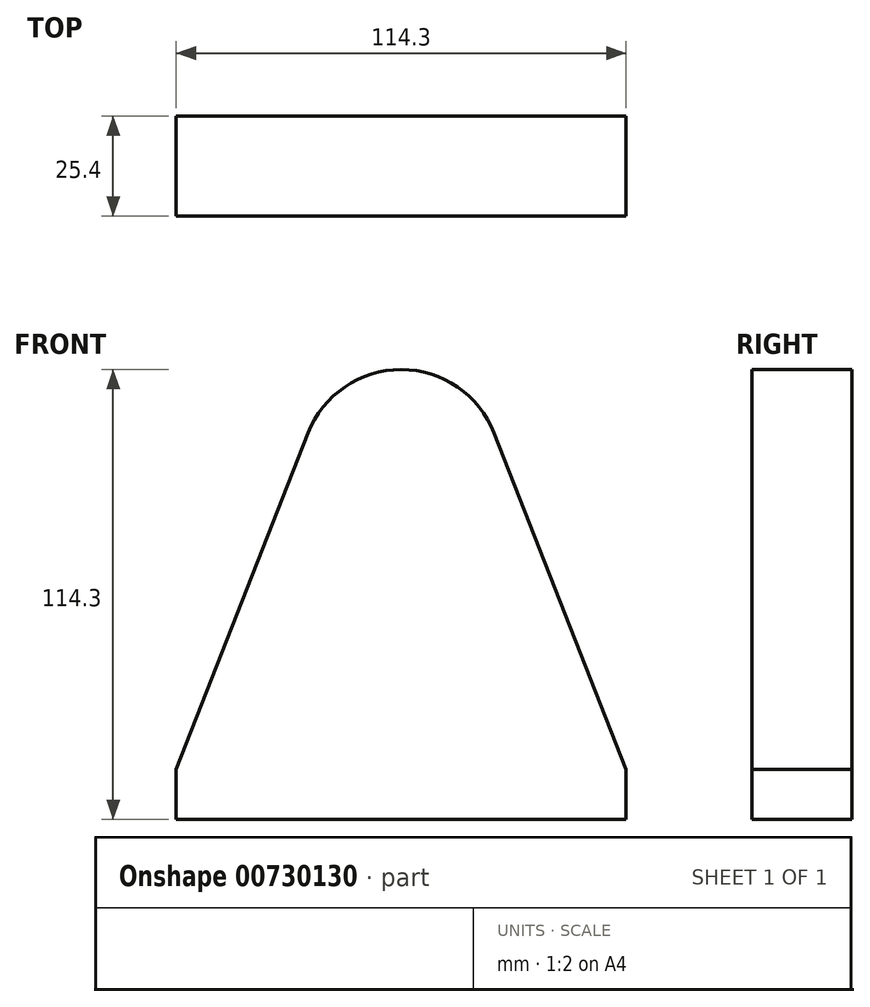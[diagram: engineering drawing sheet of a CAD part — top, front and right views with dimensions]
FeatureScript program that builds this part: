
annotation { "Feature Type Name" : "Feature", "Feature Type Description" : "" }
export const myFeature = defineFeature(function(context is Context, id is Id, definition is map)
    precondition{}
    {
        {
            var Q0;
            Q0=qCreatedBy(makeId("Front.planeOp"),FACE);
            var sketch = newSketch(context, id + "F0", { "sketchPlane" : qUnion([Q0])});
            skArc(sketch, "E0", {"start": v(23.65, 9.27) * mm, "mid": v(0, 25.4) * mm, "end": v(-23.65, 9.27) * mm});
            skLineSegment(sketch, "E1", {"start": v(-57.15, -88.9) * mm, "end": v(57.15, -88.9) * mm});
            skLineSegment(sketch, "E2", {"start": v(0, 0) * mm, "end": v(0, -88.9) * mm});
            skLineSegment(sketch, "E3", {"start": v(-57.15, -88.9) * mm, "end": v(-57.15, -76.2) * mm});
            skLineSegment(sketch, "E4", {"start": v(57.15, -88.9) * mm, "end": v(57.15, -76.2) * mm});
            skLineSegment(sketch, "E5", {"start": v(-23.65, 9.27) * mm, "end": v(-57.15, -76.2) * mm});
            skLineSegment(sketch, "E6", {"start": v(23.65, 9.27) * mm, "end": v(57.15, -76.2) * mm});
            skSolve(sketch);
        }
        {
            var Q0;
            Q0=makeQuery(id+"FaXUkO058kIDrxt_0.opExtrude","CAP_FACE",FACE,{"disambiguationData":[OSD([sQuery(id+"F0.wireOp",EDGE,"E0"),sQuery(id+"F0.wireOp",EDGE,"wo0sS95r-AHTT-0R2M-1qgF-BHLM5WRwD2go"),sQuery(id+"F0.wireOp",EDGE,"E1"),sQuery(id+"F0.wireOp",EDGE,"p98Flptp-fh9u-BcCi-NBaJ-qq9l6Gik5f4n")])],"isStart":false});
            var sketch = newSketch(context, id + "F1", { "sketchPlane" : qUnion([Q0])});
            skSolve(sketch);
        }
        {
            var Q0;
            Q0 = qSketchRegion(id + "F1", true);
            var Q1;
            Q1 = qSketchRegion(id + "F0", true);
            extrude(context, id + "F2", {"entities" : qUnion([Q0, Q1]), "depth" : 25.4 * mm, "offsetDistance" : 25.4 * mm});
        }
    });
